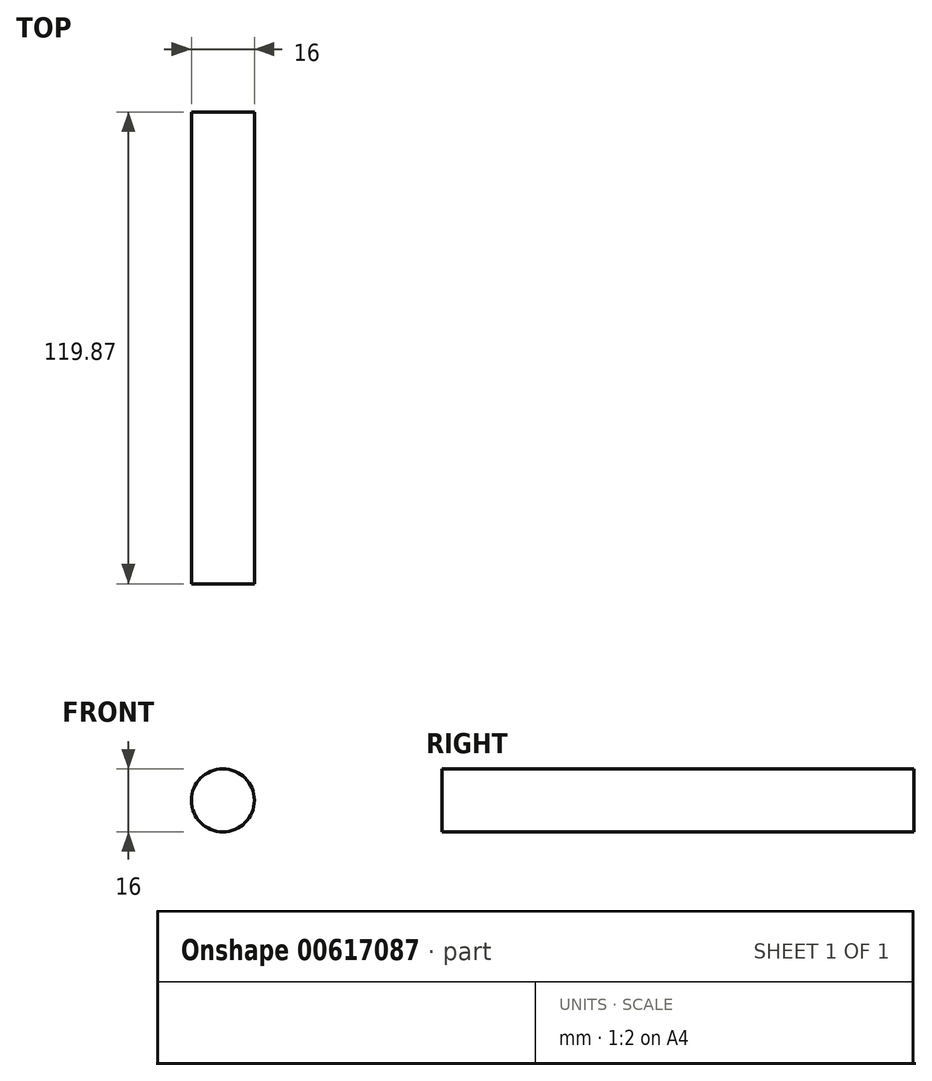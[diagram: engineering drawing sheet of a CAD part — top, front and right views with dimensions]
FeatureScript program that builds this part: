
annotation { "Feature Type Name" : "Feature", "Feature Type Description" : "" }
export const myFeature = defineFeature(function(context is Context, id is Id, definition is map)
    precondition{}
    {
        {
            var Q0;
            Q0=qCreatedBy(makeId("Front.planeOp"),FACE);
            var sketch = newSketch(context, id + "F0", { "sketchPlane" : qUnion([Q0])});
            skCircle(sketch, "E0", {"center": v(0, 1.8) * mm, "radius": 8 * mm});
            skSolve(sketch);
        }
        {
            var Q0;
            Q0 = qSketchRegion(id + "F0", true);
            extrude(context, id + "F1", {"entities" : qUnion([Q0]), "depth" : 119.87 * mm, "offsetDistance" : 25 * mm});
        }
    });
